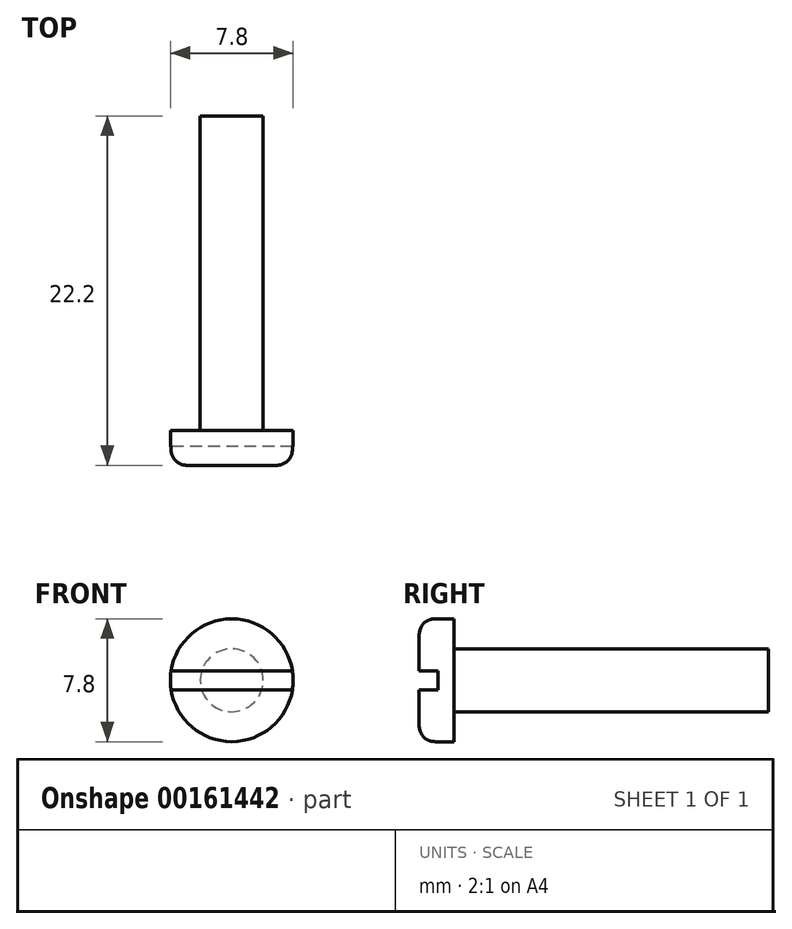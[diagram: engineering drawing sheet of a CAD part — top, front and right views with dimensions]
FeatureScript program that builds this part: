
annotation { "Feature Type Name" : "Feature", "Feature Type Description" : "" }
export const myFeature = defineFeature(function(context is Context, id is Id, definition is map)
    precondition{}
    {
        {
            var Q0;
            Q0=qCreatedBy(makeId("Front.planeOp"),FACE);
            var sketch = newSketch(context, id + "F0", { "sketchPlane" : qUnion([Q0])});
            skCircle(sketch, "E0", {"center": v(0, 0) * mm, "radius": 3.9 * mm});
            skSolve(sketch);
        }
        {
            var Q0;
            Q0=makeQuery(id+"F0.imprint","IMPRINT",FACE,{"disambiguationData":[TD([[makeQuery(id+"F0.imprint","IMPRINT",EDGE,{"derivedFrom":sQuery(id+"F0.wireOp",EDGE,"E0")}),1.0]])]});
            extrude(context, id + "F1", {"entities" : qUnion([Q0]), "oppositeDirection" : true, "depth" : 2.2 * mm});
        }
        {
            var Q0;
            Q0=makeQuery(id+"F1.opExtrude","CAP_FACE",FACE,{"disambiguationData":[OSD([sQuery(id+"F0.wireOp",EDGE,"E0")])],"isStart":true});
            fillet(context, id + "F2", {"entities" : qUnion([Q0]), "radius" : 1 * mm, "tangentPropagation" : true, "allowEdgeOverflow" : false});
        }
        {
            var Q0;
            Q0=makeQuery(id+"F1.opExtrude","CAP_FACE",FACE,{"disambiguationData":[OSD([sQuery(id+"F0.wireOp",EDGE,"E0")])],"isStart":true});
            var sketch = newSketch(context, id + "F3", { "sketchPlane" : qUnion([Q0])});
            skLineSegment(sketch, "E1.bottom", {"start": v(4, 0.6) * mm, "end": v(-4, 0.6) * mm});
            skLineSegment(sketch, "E1.top", {"start": v(4, -0.6) * mm, "end": v(-4, -0.6) * mm});
            skLineSegment(sketch, "E1.left", {"start": v(4, 0.6) * mm, "end": v(4, -0.6) * mm});
            skLineSegment(sketch, "E1.right", {"start": v(-4, 0.6) * mm, "end": v(-4, -0.6) * mm});
            skPoint(sketch, "E1.middle", {"position": v(0, 0) * mm});
            skSolve(sketch);
        }
        {
            var Q0;
            Q0=qSketchRegion(id+"F3",true);
            extrude(context, id + "F4", {"entities" : qUnion([Q0]), "operationType" : NewBodyOperationType.REMOVE, "oppositeDirection" : true, "depth" : 1.2 * mm});
        }
        {
            var Q0;
            Q0=makeQuery(id+"F1.opExtrude","CAP_FACE",FACE,{"disambiguationData":[OSD([sQuery(id+"F0.wireOp",EDGE,"E0")])],"isStart":false});
            var sketch = newSketch(context, id + "F5", { "sketchPlane" : qUnion([Q0])});
            skCircle(sketch, "E2", {"center": v(0, 0) * mm, "radius": 2 * mm});
            skSolve(sketch);
        }
        {
            var Q0;
            Q0=qSketchRegion(id+"F5",true);
            extrude(context, id + "F6", {"entities" : qUnion([Q0]), "operationType" : NewBodyOperationType.ADD, "depth" : 20 * mm});
        }
    });
